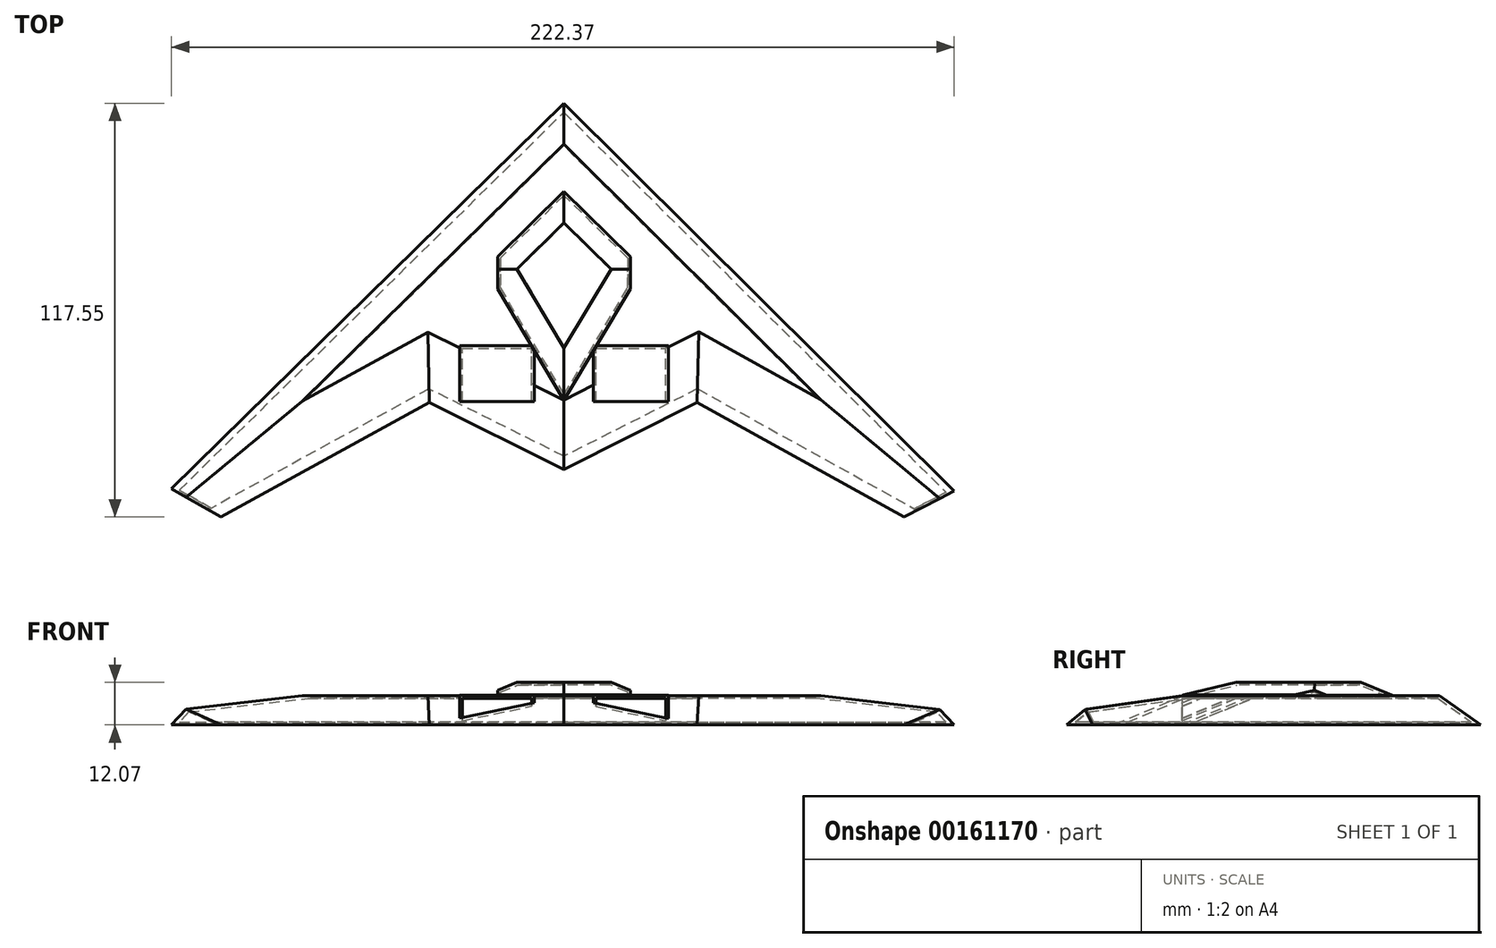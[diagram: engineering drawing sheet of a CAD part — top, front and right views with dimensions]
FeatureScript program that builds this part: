
annotation { "Feature Type Name" : "Feature", "Feature Type Description" : "" }
export const myFeature = defineFeature(function(context is Context, id is Id, definition is map)
    precondition{}
    {
        {
            var Q0;
            Q0=qCreatedBy(makeId("Top.planeOp"),FACE);
            var sketch = newSketch(context, id + "F0", { "sketchPlane" : qUnion([Q0])});
            skLineSegment(sketch, "E0", {"start": v(0, 75.18) * mm, "end": v(-76.5, 0) * mm});
            skLineSegment(sketch, "E1", {"start": v(75.62, 0) * mm, "end": v(0, 75.18) * mm});
            skPoint(sketch, "E2.start.orphan", {"position": v(37.8, -19.06) * mm});
            skPoint(sketch, "E3.end.orphan", {"position": v(-38.25, -19.06) * mm});
            skPoint(sketch, "E4.orphan", {"position": v(0, -38.12) * mm});
            skPoint(sketch, "E5.orphan", {"position": v(0, -76.24) * mm});
            skPoint(sketch, "E6.start.orphan", {"position": v(0, 0) * mm});
            skLineSegment(sketch, "E7", {"start": v(-76.5, 0) * mm, "end": v(-113.4, -39.6) * mm});
            skLineSegment(sketch, "E8", {"start": v(-113.4, -39.6) * mm, "end": v(-94.78, -50.06) * mm});
            skLineSegment(sketch, "E9", {"start": v(-94.78, -50.06) * mm, "end": v(-38.25, -19.06) * mm});
            skLineSegment(sketch, "E10", {"start": v(-38.25, -19.06) * mm, "end": v(0, -38.12) * mm});
            skLineSegment(sketch, "E11", {"start": v(0, -38.12) * mm, "end": v(37.8, -19.06) * mm});
            skLineSegment(sketch, "E12", {"start": v(75.62, 0) * mm, "end": v(115, -39.15) * mm});
            skLineSegment(sketch, "E13", {"start": v(115, -39.15) * mm, "end": v(93.84, -50.06) * mm});
            skLineSegment(sketch, "E14", {"start": v(93.84, -50.06) * mm, "end": v(37.8, -19.06) * mm});
            skSolve(sketch);
        }
        {
            var Q0;
            Q0=makeQuery(id+"F0.imprint","IMPRINT",FACE,{"disambiguationData":[TD([[makeQuery(id+"F0.imprint","IMPRINT",EDGE,{"derivedFrom":sQuery(id+"F0.wireOp",EDGE,"E0")}),1.0]])]});
            extrude(context, id + "F1", {"entities" : qUnion([Q0]), "depth" : 8.25 * mm});
        }
        {
            var Q0;
            Q0=makeQuery(id+"F1.opExtrude","CAP_EDGE",EDGE,{"disambiguationData":[OSD([sQuery(id+"F0.wireOp",EDGE,"E1"),sQuery(id+"F0.wireOp",EDGE,"E12")])],"isStart":false});
            var Q1;
            Q1=makeQuery(id+"F1.opExtrude","CAP_EDGE",EDGE,{"disambiguationData":[OSD([sQuery(id+"F0.wireOp",EDGE,"E0")])],"isStart":false});
            chamfer(context, id + "F2", {"entities" : qUnion([Q0, Q1]), "width" : 12.7 * mm, "tangentPropagation" : true});
        }
        {
            var Q0;
            Q0=makeQuery(id+"F1.opExtrude","CAP_EDGE",EDGE,{"disambiguationData":[OSD([sQuery(id+"F0.wireOp",EDGE,"E11")])],"isStart":false});
            var Q1;
            Q1=makeQuery(id+"F1.opExtrude","CAP_EDGE",EDGE,{"disambiguationData":[OSD([sQuery(id+"F0.wireOp",EDGE,"E14")])],"isStart":false});
            var Q2;
            Q2=makeQuery(id+"F1.opExtrude","CAP_EDGE",EDGE,{"disambiguationData":[OSD([sQuery(id+"F0.wireOp",EDGE,"E10")])],"isStart":false});
            var Q3;
            Q3=makeQuery(id+"F1.opExtrude","CAP_EDGE",EDGE,{"disambiguationData":[OSD([sQuery(id+"F0.wireOp",EDGE,"E9")])],"isStart":false});
            chamfer(context, id + "F3", {"entities" : qUnion([Q0, Q1, Q2, Q3]), "chamferType" : ChamferType.OFFSET_ANGLE, "width" : 20.32 * mm, "oppositeDirection" : false, "angle" : 25 * degree, "tangentPropagation" : true});
        }
        {
            var Q0;
            Q0=makeQuery(id+"F1.opExtrude","CAP_FACE",FACE,{"disambiguationData":[OSD([sQuery(id+"F0.wireOp",EDGE,"E0"),sQuery(id+"F0.wireOp",EDGE,"E1"),sQuery(id+"F0.wireOp",EDGE,"E7"),sQuery(id+"F0.wireOp",EDGE,"E8"),sQuery(id+"F0.wireOp",EDGE,"E9"),sQuery(id+"F0.wireOp",EDGE,"E10"),sQuery(id+"F0.wireOp",EDGE,"E11"),sQuery(id+"F0.wireOp",EDGE,"E12"),sQuery(id+"F0.wireOp",EDGE,"E13"),sQuery(id+"F0.wireOp",EDGE,"E14")])],"isStart":false});
            var sketch = newSketch(context, id + "F4", { "sketchPlane" : qUnion([Q0])});
            skPoint(sketch, "E15.orphan", {"position": v(0, 0) * mm});
            skPoint(sketch, "E16.end.orphan", {"position": v(-0.05, -15.4) * mm});
            skPoint(sketch, "E17.start.orphan", {"position": v(-0.03, -7.7) * mm});
            skPoint(sketch, "E18.start.orphan", {"position": v(0, 43.82) * mm});
            skLineSegment(sketch, "E19", {"start": v(0, 43.82) * mm, "end": v(-18.86, 25.28) * mm});
            skLineSegment(sketch, "E20", {"start": v(18.89, 25.28) * mm, "end": v(0, 43.82) * mm});
            skLineSegment(sketch, "E21", {"start": v(18.89, 25.28) * mm, "end": v(18.89, 16.19) * mm});
            skLineSegment(sketch, "E22", {"start": v(-18.86, 25.28) * mm, "end": v(-18.86, 16.19) * mm});
            skLineSegment(sketch, "E23", {"start": v(18.89, 16.19) * mm, "end": v(-0.05, -15.4) * mm});
            skLineSegment(sketch, "E24", {"start": v(-18.86, 16.19) * mm, "end": v(-0.05, -15.4) * mm});
            skSolve(sketch);
        }
        {
            var Q0;
            Q0=makeQuery(id+"F4.imprint","IMPRINT",FACE,{"disambiguationData":[TD([[makeQuery(id+"F4.imprint","IMPRINT",EDGE,{"derivedFrom":sQuery(id+"F4.wireOp",EDGE,"E19")}),1.0]])]});
            extrude(context, id + "F5", {"entities" : qUnion([Q0]), "operationType" : NewBodyOperationType.ADD, "depth" : 3.8 * mm});
        }
        {
            var Q0;
            Q0=makeQuery(id+"F5.opExtrude","CAP_EDGE",EDGE,{"disambiguationData":[OSD([sQuery(id+"F4.wireOp",EDGE,"E19")])],"isStart":false});
            var Q1;
            Q1=makeQuery(id+"F5.opExtrude","CAP_EDGE",EDGE,{"disambiguationData":[OSD([sQuery(id+"F4.wireOp",EDGE,"E20")])],"isStart":false});
            chamfer(context, id + "F6", {"entities" : qUnion([Q0, Q1]), "chamferType" : ChamferType.OFFSET_ANGLE, "width" : 6.35 * mm, "oppositeDirection" : false, "angle" : 30 * degree, "tangentPropagation" : true});
        }
        {
            var Q0;
            Q0=makeQuery(id+"F5.opExtrude","CAP_EDGE",EDGE,{"disambiguationData":[OSD([sQuery(id+"F4.wireOp",EDGE,"E24")])],"isStart":false});
            var Q1;
            Q1=makeQuery(id+"F5.opExtrude","CAP_EDGE",EDGE,{"disambiguationData":[OSD([sQuery(id+"F4.wireOp",EDGE,"E23")])],"isStart":false});
            chamfer(context, id + "F7", {"entities" : qUnion([Q0, Q1]), "chamferType" : ChamferType.OFFSET_ANGLE, "width" : 7.62 * mm, "oppositeDirection" : false, "angle" : 25 * degree, "tangentPropagation" : true});
        }
        {
            var Q0;
            Q0=qCreatedBy(makeId("Front.planeOp"),FACE);
            var sketch = newSketch(context, id + "F8", { "sketchPlane" : qUnion([Q0])});
            skLineSegment(sketch, "E25.bottom", {"start": v(29.69, 8.42) * mm, "end": v(8.39, 8.42) * mm});
            skLineSegment(sketch, "E25.left", {"start": v(29.69, 8.42) * mm, "end": v(29.69, 0) * mm});
            skLineSegment(sketch, "E25.right", {"start": v(-29.69, 8.42) * mm, "end": v(-29.69, 0) * mm});
            skPoint(sketch, "E25.middle", {"position": v(0, 0) * mm});
            skLineSegment(sketch, "E26", {"start": v(-29.69, 0) * mm, "end": v(-8.39, 0) * mm});
            skLineSegment(sketch, "E27", {"start": v(8.39, 8.42) * mm, "end": v(8.39, 0) * mm});
            skLineSegment(sketch, "E28", {"start": v(-8.39, 8.42) * mm, "end": v(-8.39, 0) * mm});
            skPoint(sketch, "E29.orphan", {"position": v(-29.69, -8.42) * mm});
            skPoint(sketch, "E30.orphan", {"position": v(29.69, -8.42) * mm});
            skLineSegment(sketch, "E31.trimOffspring", {"start": v(-8.39, 8.42) * mm, "end": v(-29.69, 8.42) * mm});
            skLineSegment(sketch, "E32.trimOffspring", {"start": v(8.39, 0) * mm, "end": v(29.69, 0) * mm});
            skSolve(sketch);
        }
        {
            var Q0;
            Q0=makeQuery(id+"F8.imprint","IMPRINT",FACE,{"disambiguationData":[TD([[makeQuery(id+"F8.imprint","IMPRINT",EDGE,{"derivedFrom":sQuery(id+"F8.wireOp",EDGE,"E25.bottom")}),1.0]])]});
            var Q1;
            Q1=makeQuery(id+"F8.imprint","IMPRINT",FACE,{"disambiguationData":[TD([[makeQuery(id+"F8.imprint","IMPRINT",EDGE,{"derivedFrom":sQuery(id+"F8.wireOp",EDGE,"E25.right")}),1.0]])]});
            extrude(context, id + "F9", {"entities" : qUnion([Q0, Q1]), "operationType" : NewBodyOperationType.ADD, "depth" : 15.88 * mm});
        }
        {
            var Q0;
            Q0=makeQuery(id+"F9.opExtrude","CAP_FACE",FACE,{"disambiguationData":[OSD([sQuery(id+"F8.wireOp",EDGE,"E25.bottom"),sQuery(id+"F8.wireOp",EDGE,"E25.left"),sQuery(id+"F8.wireOp",EDGE,"E27"),sQuery(id+"F8.wireOp",EDGE,"E32.trimOffspring")])],"isStart":false});
            var Q1;
            Q1=makeQuery(id+"F9.opExtrude","CAP_FACE",FACE,{"disambiguationData":[OSD([sQuery(id+"F8.wireOp",EDGE,"E25.right"),sQuery(id+"F8.wireOp",EDGE,"E28"),sQuery(id+"F8.wireOp",EDGE,"E26"),sQuery(id+"F8.wireOp",EDGE,"E31.trimOffspring")])],"isStart":false});
            shell(context, id + "F10", {"entities" : qUnion([Q0, Q1]), "thickness" : 0.76 * mm});
        }
    });
